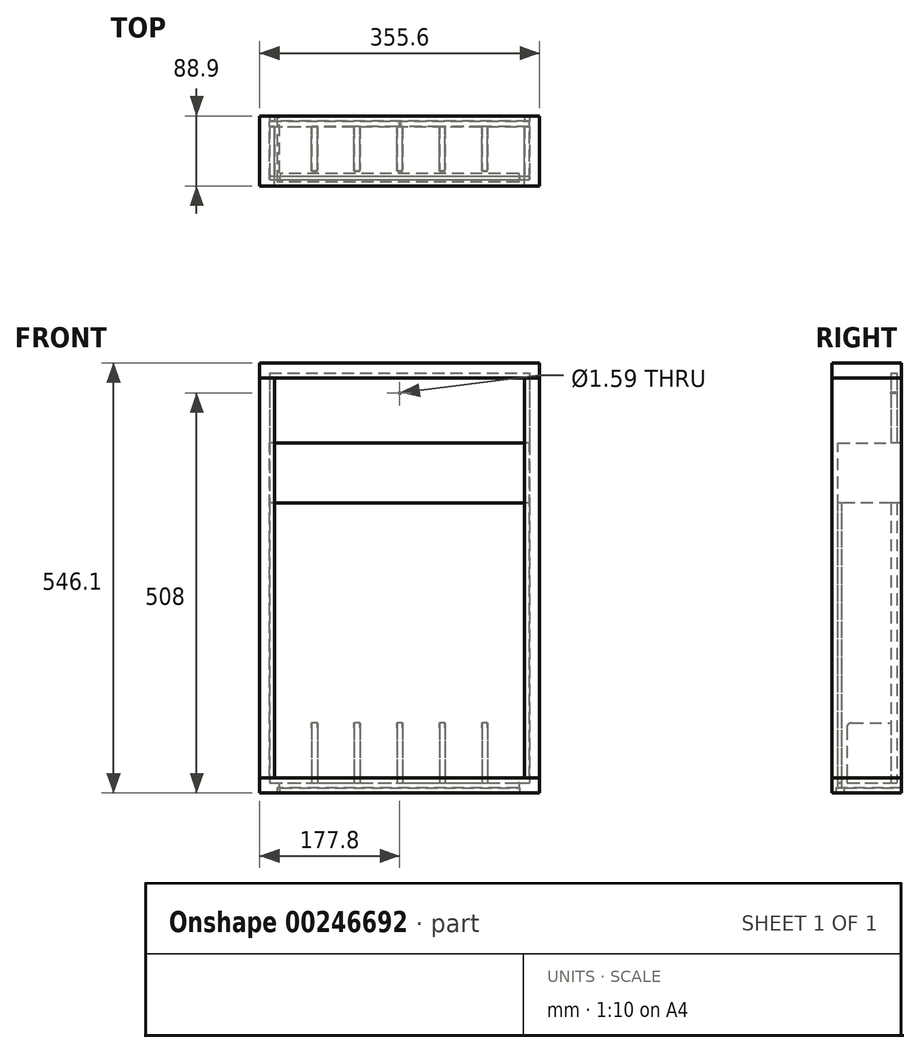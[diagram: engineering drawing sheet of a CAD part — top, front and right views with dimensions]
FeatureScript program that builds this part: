
annotation { "Feature Type Name" : "Feature", "Feature Type Description" : "" }
export const myFeature = defineFeature(function(context is Context, id is Id, definition is map)
    precondition{}
    {
        {
            var Q0;
            Q0=qCreatedBy(makeId("Top.planeOp"),FACE);
            var sketch = newSketch(context, id + "F0", { "sketchPlane" : qUnion([Q0])});
            skLineSegment(sketch, "E0.bottom", {"start": v(0, 0) * mm, "end": v(355.6, 0) * mm});
            skLineSegment(sketch, "E0.top", {"start": v(0, 88.9) * mm, "end": v(355.6, 88.9) * mm});
            skLineSegment(sketch, "E0.left", {"start": v(0, 0) * mm, "end": v(0, 88.9) * mm});
            skLineSegment(sketch, "E0.right", {"start": v(355.6, 0) * mm, "end": v(355.6, 88.9) * mm});
            skSolve(sketch);
        }
        {
            var Q0;
            Q0 = qSketchRegion(id + "F0", true);
            extrude(context, id + "F1", {"entities" : qUnion([Q0]), "depth" : 19.05 * mm});
        }
        {
            var Q0;
            Q0=makeQuery(id+"F1.opExtrude","CAP_FACE",FACE,{"disambiguationData":[OSD([sQuery(id+"F0.wireOp",EDGE,"E0.bottom"),sQuery(id+"F0.wireOp",EDGE,"E0.top"),sQuery(id+"F0.wireOp",EDGE,"E0.left"),sQuery(id+"F0.wireOp",EDGE,"E0.right")])],"isStart":false});
            var sketch = newSketch(context, id + "F2", { "sketchPlane" : qUnion([Q0])});
            skLineSegment(sketch, "E1.bottom", {"start": v(0, 0) * mm, "end": v(19.05, 0) * mm});
            skLineSegment(sketch, "E1.top", {"start": v(0, 88.9) * mm, "end": v(19.05, 88.9) * mm});
            skLineSegment(sketch, "E1.left", {"start": v(0, 0) * mm, "end": v(0, 88.9) * mm});
            skLineSegment(sketch, "E1.right", {"start": v(19.05, 0) * mm, "end": v(19.05, 88.9) * mm});
            skLineSegment(sketch, "E2.bottom", {"start": v(355.6, 0) * mm, "end": v(336.55, 0) * mm});
            skLineSegment(sketch, "E2.top", {"start": v(355.6, 88.9) * mm, "end": v(336.55, 88.9) * mm});
            skLineSegment(sketch, "E2.left", {"start": v(355.6, 0) * mm, "end": v(355.6, 88.9) * mm});
            skLineSegment(sketch, "E2.right", {"start": v(336.55, 0) * mm, "end": v(336.55, 88.9) * mm});
            skSolve(sketch);
        }
        {
            var Q0;
            Q0 = qSketchRegion(id + "F2", true);
            extrude(context, id + "F3", {"entities" : qUnion([Q0]), "depth" : 508 * mm});
        }
        {
            var Q0;
            Q0=makeQuery(id+"F3.opExtrude","CAP_FACE",FACE,{"disambiguationData":[OSD([sQuery(id+"F2.wireOp",EDGE,"E1.bottom"),sQuery(id+"F2.wireOp",EDGE,"E1.top"),sQuery(id+"F2.wireOp",EDGE,"E1.left"),sQuery(id+"F2.wireOp",EDGE,"E1.right")])],"isStart":false});
            var sketch = newSketch(context, id + "F4", { "sketchPlane" : qUnion([Q0])});
            skLineSegment(sketch, "E3.bottom", {"start": v(0, 0) * mm, "end": v(355.6, 0) * mm});
            skLineSegment(sketch, "E3.top", {"start": v(0, 88.9) * mm, "end": v(355.6, 88.9) * mm});
            skLineSegment(sketch, "E3.left", {"start": v(0, 0) * mm, "end": v(0, 88.9) * mm});
            skLineSegment(sketch, "E3.right", {"start": v(355.6, 0) * mm, "end": v(355.6, 88.9) * mm});
            skSolve(sketch);
        }
        {
            var Q0;
            Q0 = qSketchRegion(id + "F4", true);
            extrude(context, id + "F5", {"entities" : qUnion([Q0]), "depth" : 19.05 * mm});
        }
        {
            var Q0;
            Q0=makeQuery(id+"F3.opExtrude","SWEPT_FACE",FACE,{"disambiguationData":[OSD([sQuery(id+"F2.wireOp",EDGE,"E2.top")])]});
            cPlane(context, id + "F6", {"entities" : qUnion([Q0]), "cplaneType" : CPlaneType.OFFSET, "offset" : 6.35 * mm, "oppositeDirection" : true, "width" : 152.4 * mm, "height" : 152.4 * mm});
        }
        {
            var Q0;
            Q0=qCreatedBy(id+"F6.planeOp",FACE);
            var sketch = newSketch(context, id + "F7", { "sketchPlane" : qUnion([Q0])});
            skLineSegment(sketch, "E4.bottom", {"start": v(-12.7, 533.4) * mm, "end": v(-342.9, 533.4) * mm});
            skLineSegment(sketch, "E4.top", {"start": v(-12.7, 12.7) * mm, "end": v(-342.9, 12.7) * mm});
            skLineSegment(sketch, "E4.left", {"start": v(-12.7, 533.4) * mm, "end": v(-12.7, 12.7) * mm});
            skLineSegment(sketch, "E4.right", {"start": v(-342.9, 533.4) * mm, "end": v(-342.9, 12.7) * mm});
            skSolve(sketch);
        }
        {
            var Q0;
            Q0 = qSketchRegion(id + "F7", true);
            extrude(context, id + "F8", {"entities" : qUnion([Q0]), "oppositeDirection" : true, "depth" : 7.24 * mm});
        }
        {
            var Q0;
            Q0=makeQuery(id+"F8.opExtrude","SWEPT_BODY",BODY,{"disambiguationData":[OSD([sQuery(id+"F7.wireOp",EDGE,"E4.bottom"),sQuery(id+"F7.wireOp",EDGE,"E4.top"),sQuery(id+"F7.wireOp",EDGE,"E4.left"),sQuery(id+"F7.wireOp",EDGE,"E4.right")])]});
            var Q1;
            Q1=makeQuery(id+"F5.opExtrude","SWEPT_BODY",BODY,{"disambiguationData":[OSD([sQuery(id+"F4.wireOp",EDGE,"E3.bottom"),sQuery(id+"F4.wireOp",EDGE,"E3.top"),sQuery(id+"F4.wireOp",EDGE,"E3.left"),sQuery(id+"F4.wireOp",EDGE,"E3.right")])]});
            var Q2;
            Q2=makeQuery(id+"F3.opExtrude","SWEPT_BODY",BODY,{"disambiguationData":[OSD([sQuery(id+"F2.wireOp",EDGE,"E2.bottom"),sQuery(id+"F2.wireOp",EDGE,"E2.top"),sQuery(id+"F2.wireOp",EDGE,"E2.left"),sQuery(id+"F2.wireOp",EDGE,"E2.right")])]});
            var Q3;
            Q3=makeQuery(id+"F3.opExtrude","SWEPT_BODY",BODY,{"disambiguationData":[OSD([sQuery(id+"F2.wireOp",EDGE,"E1.bottom"),sQuery(id+"F2.wireOp",EDGE,"E1.top"),sQuery(id+"F2.wireOp",EDGE,"E1.left"),sQuery(id+"F2.wireOp",EDGE,"E1.right")])]});
            var Q4;
            Q4=makeQuery(id+"F1.opExtrude","SWEPT_BODY",BODY,{"disambiguationData":[OSD([sQuery(id+"F0.wireOp",EDGE,"E0.bottom"),sQuery(id+"F0.wireOp",EDGE,"E0.top"),sQuery(id+"F0.wireOp",EDGE,"E0.left"),sQuery(id+"F0.wireOp",EDGE,"E0.right")])]});
            booleanBodies(context, id + "F9", {"operationType" : BooleanOperationType.SUBTRACTION, "tools" : qUnion([Q0]), "targets" : qUnion([Q1, Q2, Q3, Q4]), "keepTools" : true});
        }
        {
            var Q0;
            Q0=makeQuery(id+"F1.opExtrude","CAP_FACE",FACE,{"disambiguationData":[OSD([sQuery(id+"F0.wireOp",EDGE,"E0.bottom"),sQuery(id+"F0.wireOp",EDGE,"E0.top"),sQuery(id+"F0.wireOp",EDGE,"E0.left"),sQuery(id+"F0.wireOp",EDGE,"E0.right")])],"isStart":false});
            var sketch = newSketch(context, id + "F10", { "sketchPlane" : qUnion([Q0])});
            skLineSegment(sketch, "E5.bottom", {"start": v(65.93, 19.05) * mm, "end": v(73.17, 19.05) * mm});
            skLineSegment(sketch, "E5.top", {"start": v(65.93, 75.31) * mm, "end": v(73.17, 75.31) * mm});
            skLineSegment(sketch, "E5.left", {"start": v(65.93, 19.05) * mm, "end": v(65.93, 75.31) * mm});
            skLineSegment(sketch, "E5.right", {"start": v(73.17, 19.05) * mm, "end": v(73.17, 75.31) * mm});
            skLineSegment(sketch, "E6.bottom", {"start": v(120.06, 19.05) * mm, "end": v(127.3, 19.05) * mm});
            skLineSegment(sketch, "E6.top", {"start": v(120.06, 75.31) * mm, "end": v(127.3, 75.31) * mm});
            skLineSegment(sketch, "E6.left", {"start": v(120.06, 19.05) * mm, "end": v(120.06, 75.31) * mm});
            skLineSegment(sketch, "E6.right", {"start": v(127.3, 19.05) * mm, "end": v(127.3, 75.31) * mm});
            skLineSegment(sketch, "E7.bottom", {"start": v(174.18, 19.05) * mm, "end": v(181.42, 19.05) * mm});
            skLineSegment(sketch, "E7.top", {"start": v(174.18, 75.31) * mm, "end": v(181.42, 75.31) * mm});
            skLineSegment(sketch, "E7.left", {"start": v(174.18, 19.05) * mm, "end": v(174.18, 75.31) * mm});
            skLineSegment(sketch, "E7.right", {"start": v(181.42, 19.05) * mm, "end": v(181.42, 75.31) * mm});
            skLineSegment(sketch, "E8.bottom", {"start": v(228.3, 19.05) * mm, "end": v(235.54, 19.05) * mm});
            skLineSegment(sketch, "E8.top", {"start": v(228.3, 75.31) * mm, "end": v(235.54, 75.31) * mm});
            skLineSegment(sketch, "E8.left", {"start": v(228.3, 19.05) * mm, "end": v(228.3, 75.31) * mm});
            skLineSegment(sketch, "E8.right", {"start": v(235.54, 19.05) * mm, "end": v(235.54, 75.31) * mm});
            skLineSegment(sketch, "E9.bottom", {"start": v(282.43, 19.05) * mm, "end": v(289.67, 19.05) * mm});
            skLineSegment(sketch, "E9.top", {"start": v(282.43, 75.31) * mm, "end": v(289.67, 75.31) * mm});
            skLineSegment(sketch, "E9.left", {"start": v(282.43, 19.05) * mm, "end": v(282.43, 75.31) * mm});
            skLineSegment(sketch, "E9.right", {"start": v(289.67, 19.05) * mm, "end": v(289.67, 75.31) * mm});
            skLineSegment(sketch, "E10.0", {"start": v(19.05, 0) * mm, "end": v(19.05, 75.31) * mm, "construction": true});
            skLineSegment(sketch, "E10.1", {"start": v(336.55, 0) * mm, "end": v(336.55, 75.31) * mm, "construction": true});
            skLineSegment(sketch, "E11", {"start": v(65.93, 19.05) * mm, "end": v(19.05, 19.05) * mm, "construction": true});
            skLineSegment(sketch, "E12", {"start": v(73.17, 19.05) * mm, "end": v(120.06, 19.05) * mm, "construction": true});
            skLineSegment(sketch, "E13", {"start": v(127.3, 19.05) * mm, "end": v(174.18, 19.05) * mm, "construction": true});
            skLineSegment(sketch, "E14", {"start": v(181.42, 19.05) * mm, "end": v(228.3, 19.05) * mm, "construction": true});
            skLineSegment(sketch, "E15", {"start": v(235.54, 19.05) * mm, "end": v(282.43, 19.05) * mm, "construction": true});
            skLineSegment(sketch, "E16", {"start": v(289.67, 19.05) * mm, "end": v(336.55, 19.05) * mm, "construction": true});
            skSolve(sketch);
        }
        {
            var Q0;
            Q0 = qSketchRegion(id + "F10", true);
            extrude(context, id + "F11", {"entities" : qUnion([Q0]), "depth" : 69.85 * mm, "hasSecondDirection" : true, "secondDirectionOppositeDirection" : true, "secondDirectionDepth" : 6.35 * mm});
        }
        {
            var Q0;
            Q0=makeQuery(id+"F11.opExtrude","SWEPT_BODY",BODY,{"disambiguationData":[OSD([sQuery(id+"F10.wireOp",EDGE,"E9.bottom"),sQuery(id+"F10.wireOp",EDGE,"E9.top"),sQuery(id+"F10.wireOp",EDGE,"E9.left"),sQuery(id+"F10.wireOp",EDGE,"E9.right")])]});
            var Q1;
            Q1=makeQuery(id+"F11.opExtrude","SWEPT_BODY",BODY,{"disambiguationData":[OSD([sQuery(id+"F10.wireOp",EDGE,"E8.bottom"),sQuery(id+"F10.wireOp",EDGE,"E8.top"),sQuery(id+"F10.wireOp",EDGE,"E8.left"),sQuery(id+"F10.wireOp",EDGE,"E8.right")])]});
            var Q2;
            Q2=makeQuery(id+"F11.opExtrude","SWEPT_BODY",BODY,{"disambiguationData":[OSD([sQuery(id+"F10.wireOp",EDGE,"E7.bottom"),sQuery(id+"F10.wireOp",EDGE,"E7.top"),sQuery(id+"F10.wireOp",EDGE,"E7.left"),sQuery(id+"F10.wireOp",EDGE,"E7.right")])]});
            var Q3;
            Q3=makeQuery(id+"F11.opExtrude","SWEPT_BODY",BODY,{"disambiguationData":[OSD([sQuery(id+"F10.wireOp",EDGE,"E6.bottom"),sQuery(id+"F10.wireOp",EDGE,"E6.top"),sQuery(id+"F10.wireOp",EDGE,"E6.left"),sQuery(id+"F10.wireOp",EDGE,"E6.right")])]});
            var Q4;
            Q4=makeQuery(id+"F11.opExtrude","SWEPT_BODY",BODY,{"disambiguationData":[OSD([sQuery(id+"F10.wireOp",EDGE,"E5.bottom"),sQuery(id+"F10.wireOp",EDGE,"E5.top"),sQuery(id+"F10.wireOp",EDGE,"E5.left"),sQuery(id+"F10.wireOp",EDGE,"E5.right")])]});
            var Q5;
            Q5=makeQuery(id+"F1.opExtrude","SWEPT_BODY",BODY,{"disambiguationData":[OSD([sQuery(id+"F0.wireOp",EDGE,"E0.bottom"),sQuery(id+"F0.wireOp",EDGE,"E0.top"),sQuery(id+"F0.wireOp",EDGE,"E0.left"),sQuery(id+"F0.wireOp",EDGE,"E0.right")])]});
            booleanBodies(context, id + "F12", {"operationType" : BooleanOperationType.SUBTRACTION, "tools" : qUnion([Q0, Q1, Q2, Q3, Q4]), "targets" : qUnion([Q5]), "keepTools" : true});
        }
        {
            var Q0;
            Q0=makeQuery(id+"F3.opExtrude","SWEPT_FACE",FACE,{"disambiguationData":[OSD([sQuery(id+"F2.wireOp",EDGE,"E1.bottom")])]});
            var sketch = newSketch(context, id + "F13", { "sketchPlane" : qUnion([Q0])});
            skLineSegment(sketch, "E17.bottom", {"start": v(0, 368.3) * mm, "end": v(355.6, 368.3) * mm});
            skLineSegment(sketch, "E17.top", {"start": v(0, 88.9) * mm, "end": v(355.6, 88.9) * mm});
            skLineSegment(sketch, "E17.left", {"start": v(0, 368.3) * mm, "end": v(0, 88.9) * mm});
            skLineSegment(sketch, "E17.right", {"start": v(355.6, 368.3) * mm, "end": v(355.6, 88.9) * mm});
            skSolve(sketch);
        }
        {
            var Q0;
            Q0 = qSketchRegion(id + "F13", true);
            extrude(context, id + "F14", {"entities" : qUnion([Q0]), "depth" : 1.27 * mm});
        }
        {
            var Q0;
            Q0=makeQuery(id+"F8.opExtrude","CAP_FACE",FACE,{"disambiguationData":[OSD([sQuery(id+"F7.wireOp",EDGE,"E4.bottom"),sQuery(id+"F7.wireOp",EDGE,"E4.top"),sQuery(id+"F7.wireOp",EDGE,"E4.left"),sQuery(id+"F7.wireOp",EDGE,"E4.right")])],"isStart":false});
            var sketch = newSketch(context, id + "F15", { "sketchPlane" : qUnion([Q0])});
            skLineSegment(sketch, "E18", {"start": v(177.8, 533.4) * mm, "end": v(177.8, 12.7) * mm, "construction": true});
            skCircle(sketch, "E19", {"center": v(177.8, 508) * mm, "radius": 0.8 * mm});
            skCircle(sketch, "E20", {"center": v(177.8, 442.91) * mm, "radius": 0.8 * mm});
            skSolve(sketch);
        }
        {
            var Q0;
            Q0 = qSketchRegion(id + "F15", true);
            extrude(context, id + "F16", {"entities" : qUnion([Q0]), "operationType" : NewBodyOperationType.REMOVE, "endBound" : BoundingType.UP_TO_NEXT, "oppositeDirection" : true, "depth" : 25.4 * mm});
        }
        {
            var Q0;
            Q0=makeQuery(id+"F11.opExtrude","SWEPT_FACE",FACE,{"disambiguationData":[OSD([sQuery(id+"F10.wireOp",EDGE,"E5.bottom")])]});
            cPlane(context, id + "F17", {"entities" : qUnion([Q0]), "cplaneType" : CPlaneType.OFFSET, "offset" : 6.35 * mm, "width" : 152.4 * mm, "height" : 152.4 * mm});
        }
        {
            var Q0;
            Q0=qCreatedBy(id+"F17.planeOp",FACE);
            var sketch = newSketch(context, id + "F18", { "sketchPlane" : qUnion([Q0])});
            skLineSegment(sketch, "E21.bottom", {"start": v(12.7, 12.7) * mm, "end": v(342.9, 12.7) * mm});
            skLineSegment(sketch, "E21.top", {"start": v(12.7, 444.5) * mm, "end": v(342.9, 444.5) * mm});
            skLineSegment(sketch, "E21.left", {"start": v(12.7, 12.7) * mm, "end": v(12.7, 444.5) * mm});
            skLineSegment(sketch, "E21.right", {"start": v(342.9, 12.7) * mm, "end": v(342.9, 444.5) * mm});
            skSolve(sketch);
        }
        {
            var Q0;
            Q0 = qSketchRegion(id + "F18", true);
            extrude(context, id + "F19", {"entities" : qUnion([Q0]), "depth" : 4.7 * mm});
        }
        {
            var Q0;
            Q0=makeQuery(id+"F19.opExtrude","SWEPT_BODY",BODY,{"disambiguationData":[OSD([sQuery(id+"F18.wireOp",EDGE,"E21.bottom"),sQuery(id+"F18.wireOp",EDGE,"E21.top"),sQuery(id+"F18.wireOp",EDGE,"E21.left"),sQuery(id+"F18.wireOp",EDGE,"E21.right")])]});
            var Q1;
            Q1=makeQuery(id+"F3.opExtrude","SWEPT_BODY",BODY,{"disambiguationData":[OSD([sQuery(id+"F2.wireOp",EDGE,"E1.bottom"),sQuery(id+"F2.wireOp",EDGE,"E1.top"),sQuery(id+"F2.wireOp",EDGE,"E1.left"),sQuery(id+"F2.wireOp",EDGE,"E1.right")])]});
            var Q2;
            Q2=makeQuery(id+"F1.opExtrude","SWEPT_BODY",BODY,{"disambiguationData":[OSD([sQuery(id+"F0.wireOp",EDGE,"E0.bottom"),sQuery(id+"F0.wireOp",EDGE,"E0.top"),sQuery(id+"F0.wireOp",EDGE,"E0.left"),sQuery(id+"F0.wireOp",EDGE,"E0.right")])]});
            var Q3;
            Q3=makeQuery(id+"F3.opExtrude","SWEPT_BODY",BODY,{"disambiguationData":[OSD([sQuery(id+"F2.wireOp",EDGE,"E2.bottom"),sQuery(id+"F2.wireOp",EDGE,"E2.top"),sQuery(id+"F2.wireOp",EDGE,"E2.left"),sQuery(id+"F2.wireOp",EDGE,"E2.right")])]});
            booleanBodies(context, id + "F20", {"operationType" : BooleanOperationType.SUBTRACTION, "tools" : qUnion([Q0]), "targets" : qUnion([Q1, Q2, Q3]), "keepTools" : true});
        }
        {
            var Q0;
            Q0=makeQuery(id+"F19.opExtrude","CAP_FACE",FACE,{"disambiguationData":[OSD([sQuery(id+"F18.wireOp",EDGE,"E21.bottom"),sQuery(id+"F18.wireOp",EDGE,"E21.top"),sQuery(id+"F18.wireOp",EDGE,"E21.left"),sQuery(id+"F18.wireOp",EDGE,"E21.right")])],"isStart":false});
            var sketch = newSketch(context, id + "F21", { "sketchPlane" : qUnion([Q0])});
            skLineSegment(sketch, "E22.bottom", {"start": v(12.7, 444.5) * mm, "end": v(342.9, 444.5) * mm});
            skLineSegment(sketch, "E22.top", {"start": v(12.7, 368.3) * mm, "end": v(342.9, 368.3) * mm});
            skLineSegment(sketch, "E22.left", {"start": v(12.7, 444.5) * mm, "end": v(12.7, 368.3) * mm});
            skLineSegment(sketch, "E22.right", {"start": v(342.9, 444.5) * mm, "end": v(342.9, 368.3) * mm});
            skSolve(sketch);
        }
        {
            var Q0;
            Q0 = qSketchRegion(id + "F21", true);
            extrude(context, id + "F22", {"entities" : qUnion([Q0]), "operationType" : NewBodyOperationType.REMOVE, "endBound" : BoundingType.THROUGH_ALL, "oppositeDirection" : true, "depth" : 25.4 * mm});
        }
        {
            var Q0;
            Q0=makeQuery(id+"F14.opExtrude","SWEPT_BODY",BODY,{"disambiguationData":[OSD([sQuery(id+"F13.wireOp",EDGE,"E17.bottom"),sQuery(id+"F13.wireOp",EDGE,"E17.top"),sQuery(id+"F13.wireOp",EDGE,"E17.left"),sQuery(id+"F13.wireOp",EDGE,"E17.right")])]});
            deleteBodies(context, id + "F23", {"entities" : qUnion([Q0])});
        }
        {
            var Q0;
            Q0=makeQuery(id+"F20.opBoolean","COPY",FACE,{"derivedFrom":makeQuery(id+"F19.opExtrude","SWEPT_FACE",FACE,{"disambiguationData":[OSD([sQuery(id+"F18.wireOp",EDGE,"E21.bottom")])]})});
            var sketch = newSketch(context, id + "F24", { "sketchPlane" : qUnion([Q0])});
            skLineSegment(sketch, "E23.bottom", {"start": v(330.2, 12.7) * mm, "end": v(25.4, 12.7) * mm});
            skLineSegment(sketch, "E23.top", {"start": v(330.2, 8) * mm, "end": v(25.4, 8) * mm});
            skLineSegment(sketch, "E23.left", {"start": v(330.2, 12.7) * mm, "end": v(330.2, 8) * mm});
            skLineSegment(sketch, "E23.right", {"start": v(25.4, 12.7) * mm, "end": v(25.4, 8) * mm});
            skSolve(sketch);
        }
        {
            var Q0;
            Q0 = qSketchRegion(id + "F24", true);
            extrude(context, id + "F25", {"entities" : qUnion([Q0]), "operationType" : NewBodyOperationType.REMOVE, "endBound" : BoundingType.UP_TO_NEXT, "oppositeDirection" : true, "depth" : 25.4 * mm});
        }
        {
            var Q0;
            Q0=makeQuery(id+"F1.opExtrude","CAP_FACE",FACE,{"disambiguationData":[OSD([sQuery(id+"F0.wireOp",EDGE,"E0.bottom"),sQuery(id+"F0.wireOp",EDGE,"E0.top"),sQuery(id+"F0.wireOp",EDGE,"E0.left"),sQuery(id+"F0.wireOp",EDGE,"E0.right")])],"isStart":true});
            var sketch = newSketch(context, id + "F26", { "sketchPlane" : qUnion([Q0])});
            skLineSegment(sketch, "E24.bottom", {"start": v(330.2, -5.14) * mm, "end": v(25.4, -5.14) * mm});
            skLineSegment(sketch, "E24.left", {"start": v(330.2, -5.14) * mm, "end": v(330.2, -15.56) * mm});
            skLineSegment(sketch, "E25", {"start": v(177.8, -5.14) * mm, "end": v(177.8, -8) * mm, "construction": true});
            skLineSegment(sketch, "E26", {"start": v(177.8, -15.56) * mm, "end": v(177.8, -12.7) * mm, "construction": true});
            skLineSegment(sketch, "E27", {"start": v(330.2, -15.56) * mm, "end": v(25.4, -15.56) * mm});
            skLineSegment(sketch, "E28", {"start": v(25.4, -15.56) * mm, "end": v(25.4, -88.9) * mm});
            skLineSegment(sketch, "E29", {"start": v(25.4, -88.9) * mm, "end": v(21.84, -88.9) * mm});
            skLineSegment(sketch, "E30", {"start": v(21.84, -88.9) * mm, "end": v(21.84, -5.14) * mm});
            skLineSegment(sketch, "E31", {"start": v(21.84, -5.14) * mm, "end": v(25.4, -5.14) * mm});
            skLineSegment(sketch, "E32", {"start": v(25.4, -5.14) * mm, "end": v(25.4, -10.35) * mm, "construction": true});
            skLineSegment(sketch, "E33", {"start": v(25.4, -10.35) * mm, "end": v(25.4, -15.56) * mm, "construction": true});
            skSolve(sketch);
        }
        {
            var Q0;
            Q0 = qSketchRegion(id + "F26", true);
            extrude(context, id + "F27", {"entities" : qUnion([Q0]), "operationType" : NewBodyOperationType.REMOVE, "oppositeDirection" : true, "depth" : 6.22 * mm});
        }
        {
            var Q0;
            Q0=makeQuery(id+"F27.boolean.opBoolean","COPY",EDGE,{"derivedFrom":makeQuery(id+"F27.opExtrude","SWEPT_EDGE",EDGE,{"disambiguationData":[OSD([sQuery(id+"F26.wireOp",EDGE,"E24.top"),sQuery(id+"F26.wireOp",EDGE,"E24.right")])]})});
            var Q1;
            Q1=makeQuery(id+"F27.boolean.opBoolean","COPY",EDGE,{"derivedFrom":makeQuery(id+"F27.opExtrude","SWEPT_EDGE",EDGE,{"disambiguationData":[OSD([sQuery(id+"F26.wireOp",EDGE,"E24.bottom"),sQuery(id+"F26.wireOp",EDGE,"E24.right")])]})});
            var Q2;
            Q2=makeQuery(id+"F27.boolean.opBoolean","COPY",EDGE,{"derivedFrom":makeQuery(id+"F27.opExtrude","SWEPT_EDGE",EDGE,{"disambiguationData":[OSD([sQuery(id+"F26.wireOp",EDGE,"E24.bottom"),sQuery(id+"F26.wireOp",EDGE,"E24.left")])]})});
            var Q3;
            Q3=makeQuery(id+"F27.boolean.opBoolean","COPY",EDGE,{"derivedFrom":makeQuery(id+"F27.opExtrude","SWEPT_EDGE",EDGE,{"disambiguationData":[OSD([sQuery(id+"F26.wireOp",EDGE,"E24.top"),sQuery(id+"F26.wireOp",EDGE,"E24.left")])]})});
            var Q4;
            Q4=makeQuery(id+"F25.boolean.opBoolean","COPY",EDGE,{"derivedFrom":makeQuery(id+"F25.opExtrude","SWEPT_EDGE",EDGE,{"disambiguationData":[OSD([sQuery(id+"F18.wireOp",EDGE,"E21.bottom"),sQuery(id+"F24.wireOp",EDGE,"E23.bottom"),sQuery(id+"F24.wireOp",EDGE,"E23.right")])]})});
            var Q5;
            Q5=makeQuery(id+"F25.boolean.opBoolean","COPY",EDGE,{"derivedFrom":makeQuery(id+"F25.opExtrude","SWEPT_EDGE",EDGE,{"disambiguationData":[OSD([sQuery(id+"F18.wireOp",EDGE,"E21.bottom"),sQuery(id+"F24.wireOp",EDGE,"E23.top"),sQuery(id+"F24.wireOp",EDGE,"E23.right")])]})});
            var Q6;
            Q6=makeQuery(id+"F25.boolean.opBoolean","COPY",EDGE,{"derivedFrom":makeQuery(id+"F25.opExtrude","SWEPT_EDGE",EDGE,{"disambiguationData":[OSD([sQuery(id+"F18.wireOp",EDGE,"E21.bottom"),sQuery(id+"F24.wireOp",EDGE,"E23.bottom"),sQuery(id+"F24.wireOp",EDGE,"E23.left")])]})});
            var Q7;
            Q7=makeQuery(id+"F25.boolean.opBoolean","COPY",EDGE,{"derivedFrom":makeQuery(id+"F25.opExtrude","SWEPT_EDGE",EDGE,{"disambiguationData":[OSD([sQuery(id+"F18.wireOp",EDGE,"E21.bottom"),sQuery(id+"F24.wireOp",EDGE,"E23.top"),sQuery(id+"F24.wireOp",EDGE,"E23.left")])]})});
            fillet(context, id + "F28", {"entities" : qUnion([Q0, Q1, Q2, Q3, Q4, Q5, Q6, Q7]), "radius" : 1.59 * mm, "tangentPropagation" : true, "allowEdgeOverflow" : false});
        }
        {
            var Q0;
            Q0=makeQuery(id+"F11.opExtrude","CAP_EDGE",EDGE,{"disambiguationData":[OSD([sQuery(id+"F10.wireOp",EDGE,"E5.bottom")])],"isStart":false});
            var Q1;
            Q1=makeQuery(id+"F11.opExtrude","CAP_EDGE",EDGE,{"disambiguationData":[OSD([sQuery(id+"F10.wireOp",EDGE,"E6.bottom")])],"isStart":false});
            var Q2;
            Q2=makeQuery(id+"F11.opExtrude","CAP_EDGE",EDGE,{"disambiguationData":[OSD([sQuery(id+"F10.wireOp",EDGE,"E7.bottom")])],"isStart":false});
            var Q3;
            Q3=makeQuery(id+"F11.opExtrude","CAP_EDGE",EDGE,{"disambiguationData":[OSD([sQuery(id+"F10.wireOp",EDGE,"E8.bottom")])],"isStart":false});
            var Q4;
            Q4=makeQuery(id+"F11.opExtrude","CAP_EDGE",EDGE,{"disambiguationData":[OSD([sQuery(id+"F10.wireOp",EDGE,"E9.bottom")])],"isStart":false});
            fillet(context, id + "F29", {"entities" : qUnion([Q0, Q1, Q2, Q3, Q4]), "radius" : 6.35 * mm, "tangentPropagation" : true, "allowEdgeOverflow" : false});
        }
        {
            var Q0;
            Q0=makeQuery(id+"F27.boolean.opBoolean","COPY",EDGE,{"derivedFrom":makeQuery(id+"F27.opExtrude","SWEPT_EDGE",EDGE,{"disambiguationData":[OSD([sQuery(id+"F26.wireOp",EDGE,"E30"),sQuery(id+"F26.wireOp",EDGE,"E31")])]})});
            var Q1;
            Q1=makeQuery(id+"F27.boolean.opBoolean","COPY",EDGE,{"derivedFrom":makeQuery(id+"F27.opExtrude","SWEPT_EDGE",EDGE,{"disambiguationData":[OSD([sQuery(id+"F26.wireOp",EDGE,"E27"),sQuery(id+"F26.wireOp",EDGE,"E28")])]})});
            var Q2;
            Q2=makeQuery(id+"F27.boolean.opBoolean","COPY",EDGE,{"derivedFrom":makeQuery(id+"F27.opExtrude","SWEPT_EDGE",EDGE,{"disambiguationData":[OSD([sQuery(id+"F0.wireOp",EDGE,"E0.top"),sQuery(id+"F26.wireOp",EDGE,"E29"),sQuery(id+"F26.wireOp",EDGE,"E30")])]})});
            var Q3;
            Q3=makeQuery(id+"F27.boolean.opBoolean","COPY",EDGE,{"derivedFrom":makeQuery(id+"F27.opExtrude","SWEPT_EDGE",EDGE,{"disambiguationData":[OSD([sQuery(id+"F0.wireOp",EDGE,"E0.top"),sQuery(id+"F26.wireOp",EDGE,"E28"),sQuery(id+"F26.wireOp",EDGE,"E29")])]})});
            var Q4;
            {var subQ0=sQuery(id+"F18.wireOp",EDGE,"E21.bottom");var subQ1=sQuery(id+"F18.wireOp",EDGE,"E21.left");Q4=makeQuery(id+"F20.opBoolean","COPY",EDGE,{"disambiguationData":[TD([makeQuery(id+"F19.opExtrude","SWEPT_FACE",FACE,{"disambiguationData":[OSD([subQ0])]})])],"derivedFrom":makeQuery(id+"F19.opExtrude","CAP_EDGE",EDGE,{"disambiguationData":[OSD([subQ1])],"isStart":false})});}
            var Q5;
            {var subQ0=sQuery(id+"F18.wireOp",EDGE,"E21.left");var subQ1=sQuery(id+"F18.wireOp",EDGE,"E21.bottom");Q5=makeQuery(id+"F20.opBoolean","COPY",EDGE,{"disambiguationData":[TD([makeQuery(id+"F19.opExtrude","SWEPT_FACE",FACE,{"disambiguationData":[OSD([subQ1])]})])],"derivedFrom":makeQuery(id+"F19.opExtrude","CAP_EDGE",EDGE,{"disambiguationData":[OSD([subQ0])],"isStart":true})});}
            var Q6;
            {var subQ0=sQuery(id+"F18.wireOp",EDGE,"E21.right");var subQ1=sQuery(id+"F18.wireOp",EDGE,"E21.bottom");Q6=makeQuery(id+"F20.opBoolean","COPY",EDGE,{"disambiguationData":[TD([makeQuery(id+"F19.opExtrude","SWEPT_FACE",FACE,{"disambiguationData":[OSD([subQ1])]})])],"derivedFrom":makeQuery(id+"F19.opExtrude","CAP_EDGE",EDGE,{"disambiguationData":[OSD([subQ0])],"isStart":true})});}
            var Q7;
            {var subQ0=sQuery(id+"F18.wireOp",EDGE,"E21.bottom");var subQ1=sQuery(id+"F18.wireOp",EDGE,"E21.right");Q7=makeQuery(id+"F20.opBoolean","COPY",EDGE,{"disambiguationData":[TD([makeQuery(id+"F19.opExtrude","SWEPT_FACE",FACE,{"disambiguationData":[OSD([subQ0])]})])],"derivedFrom":makeQuery(id+"F19.opExtrude","CAP_EDGE",EDGE,{"disambiguationData":[OSD([subQ1])],"isStart":false})});}
            var Q8;
            {var subQ0=sQuery(id+"F7.wireOp",EDGE,"E4.left");var subQ1=sQuery(id+"F7.wireOp",EDGE,"E4.top");Q8=makeQuery(id+"F9.opBoolean","COPY",EDGE,{"disambiguationData":[TD([makeQuery(id+"F8.opExtrude","SWEPT_FACE",FACE,{"disambiguationData":[OSD([subQ1])]})])],"derivedFrom":makeQuery(id+"F8.opExtrude","CAP_EDGE",EDGE,{"disambiguationData":[OSD([subQ0])],"isStart":true})});}
            var Q9;
            {var subQ0=sQuery(id+"F7.wireOp",EDGE,"E4.left");var subQ1=sQuery(id+"F7.wireOp",EDGE,"E4.top");Q9=makeQuery(id+"F9.opBoolean","COPY",EDGE,{"disambiguationData":[TD([makeQuery(id+"F8.opExtrude","SWEPT_FACE",FACE,{"disambiguationData":[OSD([subQ1])]})])],"derivedFrom":makeQuery(id+"F8.opExtrude","CAP_EDGE",EDGE,{"disambiguationData":[OSD([subQ0])],"isStart":false})});}
            var Q10;
            Q10=makeQuery(id+"F12.opBoolean","COPY",EDGE,{"derivedFrom":makeQuery(id+"F11.opExtrude","SWEPT_EDGE",EDGE,{"disambiguationData":[OSD([sQuery(id+"F10.wireOp",EDGE,"E5.bottom"),sQuery(id+"F10.wireOp",EDGE,"E5.left")])]})});
            var Q11;
            Q11=makeQuery(id+"F12.opBoolean","COPY",EDGE,{"derivedFrom":makeQuery(id+"F11.opExtrude","SWEPT_EDGE",EDGE,{"disambiguationData":[OSD([sQuery(id+"F10.wireOp",EDGE,"E6.bottom"),sQuery(id+"F10.wireOp",EDGE,"E6.left")])]})});
            var Q12;
            Q12=makeQuery(id+"F12.opBoolean","COPY",EDGE,{"derivedFrom":makeQuery(id+"F11.opExtrude","SWEPT_EDGE",EDGE,{"disambiguationData":[OSD([sQuery(id+"F10.wireOp",EDGE,"E7.bottom"),sQuery(id+"F10.wireOp",EDGE,"E7.left")])]})});
            var Q13;
            Q13=makeQuery(id+"F12.opBoolean","COPY",EDGE,{"derivedFrom":makeQuery(id+"F11.opExtrude","SWEPT_EDGE",EDGE,{"disambiguationData":[OSD([sQuery(id+"F10.wireOp",EDGE,"E8.bottom"),sQuery(id+"F10.wireOp",EDGE,"E8.left")])]})});
            var Q14;
            Q14=makeQuery(id+"F12.opBoolean","COPY",EDGE,{"derivedFrom":makeQuery(id+"F11.opExtrude","SWEPT_EDGE",EDGE,{"disambiguationData":[OSD([sQuery(id+"F10.wireOp",EDGE,"E9.bottom"),sQuery(id+"F10.wireOp",EDGE,"E9.left")])]})});
            var Q15;
            {var subQ0=sQuery(id+"F7.wireOp",EDGE,"E4.right");var subQ1=sQuery(id+"F7.wireOp",EDGE,"E4.top");Q15=makeQuery(id+"F9.opBoolean","COPY",EDGE,{"disambiguationData":[TD([makeQuery(id+"F8.opExtrude","SWEPT_FACE",FACE,{"disambiguationData":[OSD([subQ1])]})])],"derivedFrom":makeQuery(id+"F8.opExtrude","CAP_EDGE",EDGE,{"disambiguationData":[OSD([subQ0])],"isStart":false})});}
            var Q16;
            {var subQ0=sQuery(id+"F7.wireOp",EDGE,"E4.right");var subQ1=sQuery(id+"F7.wireOp",EDGE,"E4.top");Q16=makeQuery(id+"F9.opBoolean","COPY",EDGE,{"disambiguationData":[TD([makeQuery(id+"F8.opExtrude","SWEPT_FACE",FACE,{"disambiguationData":[OSD([subQ1])]})])],"derivedFrom":makeQuery(id+"F8.opExtrude","CAP_EDGE",EDGE,{"disambiguationData":[OSD([subQ0])],"isStart":true})});}
            var Q17;
            Q17=makeQuery(id+"F12.opBoolean","COPY",EDGE,{"derivedFrom":makeQuery(id+"F11.opExtrude","SWEPT_EDGE",EDGE,{"disambiguationData":[OSD([sQuery(id+"F10.wireOp",EDGE,"E9.bottom"),sQuery(id+"F10.wireOp",EDGE,"E9.right")])]})});
            var Q18;
            Q18=makeQuery(id+"F12.opBoolean","COPY",EDGE,{"derivedFrom":makeQuery(id+"F11.opExtrude","SWEPT_EDGE",EDGE,{"disambiguationData":[OSD([sQuery(id+"F10.wireOp",EDGE,"E8.bottom"),sQuery(id+"F10.wireOp",EDGE,"E8.right")])]})});
            var Q19;
            Q19=makeQuery(id+"F12.opBoolean","COPY",EDGE,{"derivedFrom":makeQuery(id+"F11.opExtrude","SWEPT_EDGE",EDGE,{"disambiguationData":[OSD([sQuery(id+"F10.wireOp",EDGE,"E7.bottom"),sQuery(id+"F10.wireOp",EDGE,"E7.right")])]})});
            var Q20;
            Q20=makeQuery(id+"F12.opBoolean","COPY",EDGE,{"derivedFrom":makeQuery(id+"F11.opExtrude","SWEPT_EDGE",EDGE,{"disambiguationData":[OSD([sQuery(id+"F10.wireOp",EDGE,"E6.bottom"),sQuery(id+"F10.wireOp",EDGE,"E6.right")])]})});
            var Q21;
            Q21=makeQuery(id+"F12.opBoolean","COPY",EDGE,{"derivedFrom":makeQuery(id+"F11.opExtrude","SWEPT_EDGE",EDGE,{"disambiguationData":[OSD([sQuery(id+"F10.wireOp",EDGE,"E5.bottom"),sQuery(id+"F10.wireOp",EDGE,"E5.right")])]})});
            fillet(context, id + "F30", {"entities" : qUnion([Q0, Q1, Q2, Q3, Q4, Q5, Q6, Q7, Q8, Q9, Q10, Q11, Q12, Q13, Q14, Q15, Q16, Q17, Q18, Q19, Q20, Q21]), "radius" : 1.59 * mm, "tangentPropagation" : true, "allowEdgeOverflow" : false});
        }
    });
